FCSTD DOCUMENT  (FreeCAD 0.21R33694 (Git))
Label: schematics
License: All rights reserved
LicenseURL: https://en.wikipedia.org/wiki/All_rights_reserved
objects: Sketcher::SketchObject×1
note: 1 computed .brp shape members not serialized (recipe doc carries the construction recipe); baked Part::Feature solids carry a one-line shape summary decoded from their .brp

FEATURE [Sketcher::SketchObject] Sketch
  FullyConstrained = false
  sketch-geometry (3):
    g0: LineSegment StartX=0 StartY=0 StartZ=0 EndX=-91.4939 EndY=-4.80508 EndZ=0
    g1: LineSegment StartX=-91.4939 StartY=-4.80508 StartZ=0 EndX=-100.433 EndY=100.717 EndZ=0
    g2: LineSegment StartX=0 StartY=0 StartZ=0 EndX=-100.433 EndY=100.717 EndZ=0
  constraints (10):
    c: Coincident(g0,g-1)
    c: Coincident(g1,g0)
    c: Angle(g-2,g0) = 1.62327
    c: DistanceX(g1,g0) = 100.433
    c: DistanceY(g0,g1) = 100.717
    c: Distance(g0) = 91.62
    c: Distance(g1) = 105.9
    c: Angle(g0,g1) = 1.60284
    c: Coincident(g2,g0)
    c: Coincident(g2,g1)
